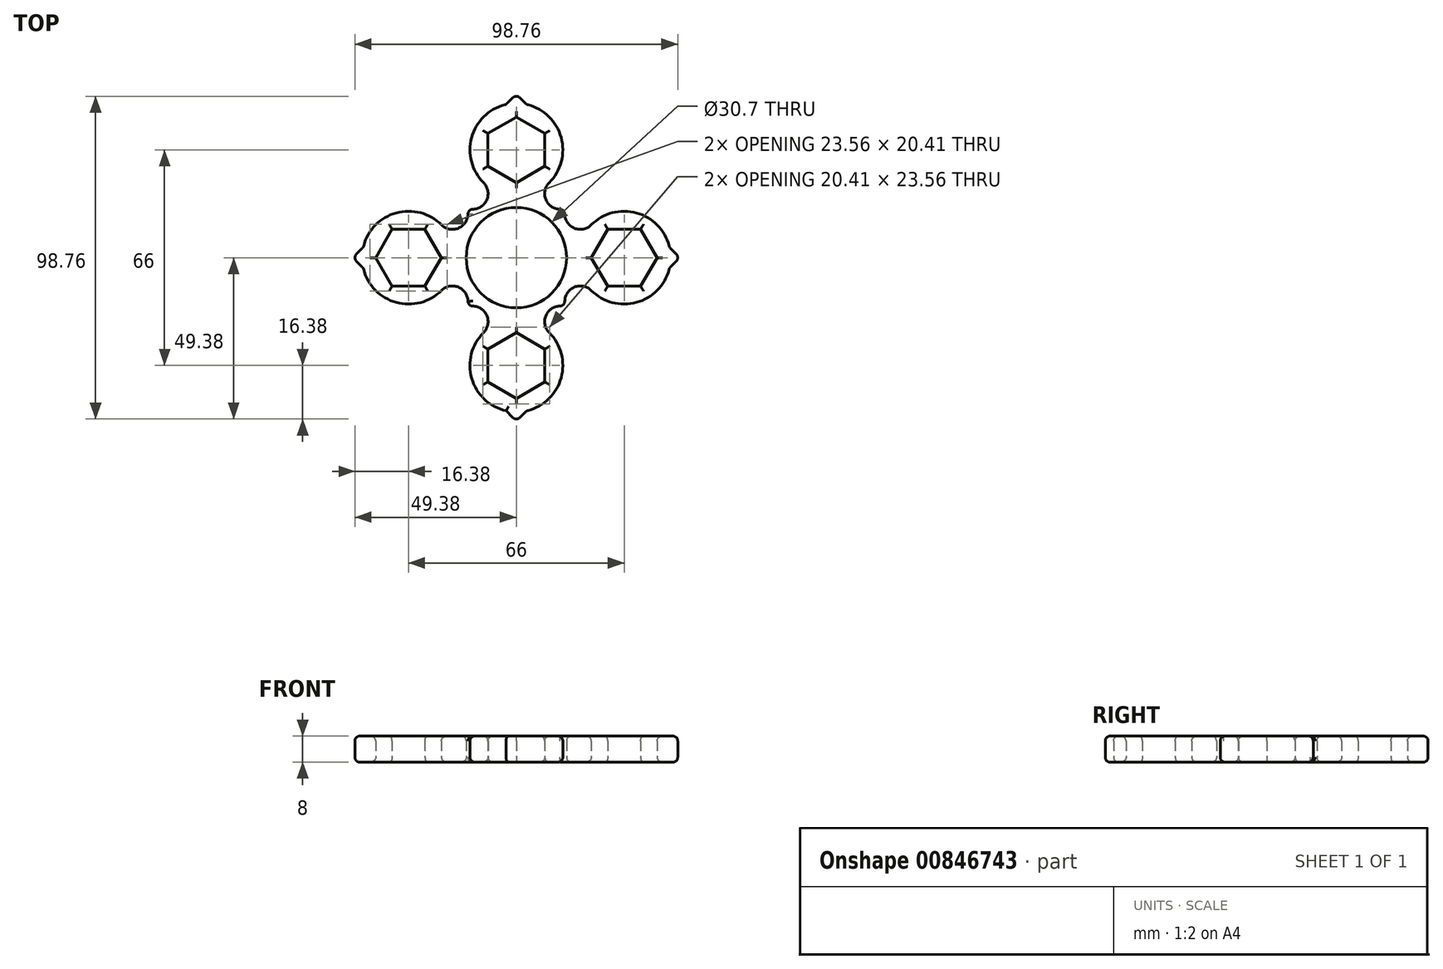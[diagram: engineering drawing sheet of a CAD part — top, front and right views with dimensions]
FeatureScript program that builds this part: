
annotation { "Feature Type Name" : "Feature", "Feature Type Description" : "" }
export const myFeature = defineFeature(function(context is Context, id is Id, definition is map)
    precondition{}
    {
        {
            var Q0;
            Q0=qCreatedBy(makeId("Top.planeOp"),FACE);
            var sketch = newSketch(context, id + "F0", { "sketchPlane" : qUnion([Q0])});
            skCircle(sketch, "E0", {"center": v(0, 0) * mm, "radius": 15.35 * mm});
            skCircle(sketch, "E1.cCircle", {"center": v(0, 0) * mm, "radius": 50 * mm, "construction": true});
            skLineSegment(sketch, "E1.0", {"start": v(0, 50) * mm, "end": v(3.14, 46.86) * mm});
            skLineSegment(sketch, "E1.1", {"start": v(50, 0) * mm, "end": v(46.86, -3.14) * mm});
            skLineSegment(sketch, "E1.2", {"start": v(0, -50) * mm, "end": v(-3.14, -46.86) * mm});
            skLineSegment(sketch, "E1.3", {"start": v(-50, 0) * mm, "end": v(-46.86, 3.14) * mm});
            skArc(sketch, "E2.cCircle", {"start": v(8.7, 27.97) * mm, "mid": v(-7.97, 39.12) * mm, "end": v(7.1, 25.9) * mm, "construction": true});
            skLineSegment(sketch, "E2.0", {"start": v(0, 22.95) * mm, "end": v(-8.7, 27.98) * mm});
            skLineSegment(sketch, "E2.1", {"start": v(-8.7, 27.98) * mm, "end": v(-8.7, 38.03) * mm});
            skLineSegment(sketch, "E2.2", {"start": v(-8.7, 38.03) * mm, "end": v(0, 43.05) * mm});
            skLineSegment(sketch, "E2.3", {"start": v(0, 43.05) * mm, "end": v(8.7, 38.03) * mm});
            skLineSegment(sketch, "E2.4", {"start": v(8.7, 38.03) * mm, "end": v(8.7, 27.97) * mm});
            skLineSegment(sketch, "E2.5", {"start": v(8.7, 27.97) * mm, "end": v(0, 22.95) * mm});
            skCircle(sketch, "E3.cCircle", {"center": v(33, 0) * mm, "radius": 10.05 * mm, "construction": true});
            skLineSegment(sketch, "E3.0", {"start": v(22.95, 0) * mm, "end": v(27.98, 8.7) * mm});
            skLineSegment(sketch, "E3.1", {"start": v(27.98, 8.7) * mm, "end": v(38.02, 8.7) * mm});
            skLineSegment(sketch, "E3.2", {"start": v(38.02, 8.7) * mm, "end": v(43.05, 0) * mm});
            skLineSegment(sketch, "E3.3", {"start": v(43.05, 0) * mm, "end": v(38.03, -8.7) * mm});
            skLineSegment(sketch, "E3.4", {"start": v(38.03, -8.7) * mm, "end": v(27.98, -8.7) * mm});
            skLineSegment(sketch, "E3.5", {"start": v(27.97, -8.7) * mm, "end": v(22.95, 0) * mm});
            skCircle(sketch, "E4.cCircle", {"center": v(0, -33) * mm, "radius": 10.05 * mm, "construction": true});
            skLineSegment(sketch, "E4.0", {"start": v(0, -22.95) * mm, "end": v(8.7, -27.97) * mm});
            skLineSegment(sketch, "E4.1", {"start": v(8.7, -27.97) * mm, "end": v(8.7, -38.02) * mm});
            skLineSegment(sketch, "E4.2", {"start": v(8.7, -38.02) * mm, "end": v(0, -43.05) * mm});
            skLineSegment(sketch, "E4.3", {"start": v(0, -43.05) * mm, "end": v(-8.7, -38.03) * mm});
            skLineSegment(sketch, "E4.4", {"start": v(-8.7, -38.03) * mm, "end": v(-8.7, -27.98) * mm});
            skLineSegment(sketch, "E4.5", {"start": v(-8.7, -27.98) * mm, "end": v(0, -22.95) * mm});
            skCircle(sketch, "E5.cCircle", {"center": v(-33, 0) * mm, "radius": 10.05 * mm, "construction": true});
            skLineSegment(sketch, "E5.0", {"start": v(-22.95, 0) * mm, "end": v(-27.98, -8.7) * mm});
            skLineSegment(sketch, "E5.1", {"start": v(-27.98, -8.7) * mm, "end": v(-38.03, -8.7) * mm});
            skLineSegment(sketch, "E5.2", {"start": v(-38.02, -8.7) * mm, "end": v(-43.05, 0) * mm});
            skLineSegment(sketch, "E5.3", {"start": v(-43.05, 0) * mm, "end": v(-38.03, 8.7) * mm});
            skLineSegment(sketch, "E5.4", {"start": v(-38.03, 8.7) * mm, "end": v(-27.97, 8.7) * mm});
            skLineSegment(sketch, "E5.5", {"start": v(-27.97, 8.7) * mm, "end": v(-22.95, 0) * mm});
            skPoint(sketch, "E6.center.orphan", {"position": v(16.5, 16.5) * mm});
            skArc(sketch, "E7", {"start": v(15.14, -15.14) * mm, "mid": v(9.43, -16.98) * mm, "end": v(10.05, -22.95) * mm});
            skArc(sketch, "E8", {"start": v(22.95, -10.05) * mm, "mid": v(16.98, -9.43) * mm, "end": v(15.14, -15.14) * mm});
            skArc(sketch, "E9", {"start": v(15.14, 15.14) * mm, "mid": v(16.98, 9.43) * mm, "end": v(22.95, 10.05) * mm});
            skArc(sketch, "E10", {"start": v(10.05, 22.95) * mm, "mid": v(9.43, 16.98) * mm, "end": v(15.14, 15.14) * mm});
            skArc(sketch, "E11", {"start": v(-22.95, 10.05) * mm, "mid": v(-16.98, 9.43) * mm, "end": v(-15.14, 15.14) * mm});
            skArc(sketch, "E12", {"start": v(-15.14, -15.14) * mm, "mid": v(-16.98, -9.43) * mm, "end": v(-22.95, -10.05) * mm});
            skArc(sketch, "E13", {"start": v(-10.05, -22.95) * mm, "mid": v(-9.43, -16.98) * mm, "end": v(-15.14, -15.14) * mm});
            skArc(sketch, "E14", {"start": v(-22.95, 10.05) * mm, "mid": v(-36.94, 13.65) * mm, "end": v(-46.86, 3.14) * mm});
            skArc(sketch, "E15", {"start": v(-10.05, -22.95) * mm, "mid": v(-13.65, -36.94) * mm, "end": v(-3.14, -46.86) * mm});
            skArc(sketch, "E16", {"start": v(22.95, -10.05) * mm, "mid": v(36.94, -13.65) * mm, "end": v(46.86, -3.14) * mm});
            skArc(sketch, "E17.trimOffspring", {"start": v(10.05, 22.95) * mm, "mid": v(13.65, 36.94) * mm, "end": v(3.14, 46.86) * mm});
            skLineSegment(sketch, "E18.trimOffspring", {"start": v(46.86, 3.14) * mm, "end": v(50, 0) * mm});
            skLineSegment(sketch, "E19.trimOffspring", {"start": v(-3.14, 46.86) * mm, "end": v(0, 50) * mm});
            skArc(sketch, "E20.trimOffspring", {"start": v(-3.14, 46.86) * mm, "mid": v(-13.65, 36.94) * mm, "end": v(-10.05, 22.95) * mm});
            skLineSegment(sketch, "E21.trimOffspring", {"start": v(-46.86, -3.14) * mm, "end": v(-50, 0) * mm});
            skLineSegment(sketch, "E22.trimOffspring", {"start": v(3.14, -46.86) * mm, "end": v(0, -50) * mm});
            skArc(sketch, "E23.trimOffspring", {"start": v(-46.86, -3.14) * mm, "mid": v(-36.94, -13.65) * mm, "end": v(-22.95, -10.05) * mm});
            skPoint(sketch, "E24.center.orphan", {"position": v(-16.5, 16.5) * mm});
            skArc(sketch, "E25.trimOffspring", {"start": v(-15.14, 15.14) * mm, "mid": v(-9.43, 16.98) * mm, "end": v(-10.05, 22.95) * mm});
            skPoint(sketch, "E26.center.orphan", {"position": v(-16.5, -16.5) * mm});
            skArc(sketch, "E27.trimOffspring", {"start": v(3.14, -46.86) * mm, "mid": v(13.65, -36.94) * mm, "end": v(10.05, -22.95) * mm});
            skLineSegment(sketch, "E28", {"start": v(10.06, -22.94) * mm, "end": v(10.05, -22.95) * mm});
            skPoint(sketch, "E29.center.orphan", {"position": v(16.5, -16.5) * mm});
            skArc(sketch, "E30.trimOffspring", {"start": v(46.86, 3.14) * mm, "mid": v(36.94, 13.65) * mm, "end": v(22.95, 10.05) * mm});
            skSolve(sketch);
        }
        {
            var Q0;
            Q0 = qSketchRegion(id + "F0", true);
            extrude(context, id + "F1", {"entities" : qUnion([Q0]), "depth" : 8 * mm, "offsetDistance" : 25 * mm});
        }
        {
            var Q0;
            Q0=makeQuery(id+"F1.opExtrude","CAP_FACE",FACE,{"disambiguationData":[OSD([sQuery(id+"F0.wireOp",EDGE,"E0"),sQuery(id+"F0.wireOp",EDGE,"E1.0"),sQuery(id+"F0.wireOp",EDGE,"E1.1"),sQuery(id+"F0.wireOp",EDGE,"E1.2"),sQuery(id+"F0.wireOp",EDGE,"E1.3"),sQuery(id+"F0.wireOp",EDGE,"E2.0"),sQuery(id+"F0.wireOp",EDGE,"E2.1"),sQuery(id+"F0.wireOp",EDGE,"E2.2"),sQuery(id+"F0.wireOp",EDGE,"E2.3"),sQuery(id+"F0.wireOp",EDGE,"E2.4"),sQuery(id+"F0.wireOp",EDGE,"E2.5"),sQuery(id+"F0.wireOp",EDGE,"E3.0"),sQuery(id+"F0.wireOp",EDGE,"E3.1"),sQuery(id+"F0.wireOp",EDGE,"E3.2"),sQuery(id+"F0.wireOp",EDGE,"E3.3"),sQuery(id+"F0.wireOp",EDGE,"E3.4"),sQuery(id+"F0.wireOp",EDGE,"E3.5"),sQuery(id+"F0.wireOp",EDGE,"E4.0"),sQuery(id+"F0.wireOp",EDGE,"E4.1"),sQuery(id+"F0.wireOp",EDGE,"E4.2"),sQuery(id+"F0.wireOp",EDGE,"E4.3"),sQuery(id+"F0.wireOp",EDGE,"E4.4"),sQuery(id+"F0.wireOp",EDGE,"E4.5"),sQuery(id+"F0.wireOp",EDGE,"E5.0"),sQuery(id+"F0.wireOp",EDGE,"E5.1"),sQuery(id+"F0.wireOp",EDGE,"E5.2"),sQuery(id+"F0.wireOp",EDGE,"E5.3"),sQuery(id+"F0.wireOp",EDGE,"E5.4"),sQuery(id+"F0.wireOp",EDGE,"E5.5"),sQuery(id+"F0.wireOp",EDGE,"E7"),sQuery(id+"F0.wireOp",EDGE,"E8"),sQuery(id+"F0.wireOp",EDGE,"E9"),sQuery(id+"F0.wireOp",EDGE,"E10"),sQuery(id+"F0.wireOp",EDGE,"E11"),sQuery(id+"F0.wireOp",EDGE,"E12"),sQuery(id+"F0.wireOp",EDGE,"E13"),sQuery(id+"F0.wireOp",EDGE,"E14"),sQuery(id+"F0.wireOp",EDGE,"E15"),sQuery(id+"F0.wireOp",EDGE,"E16"),sQuery(id+"F0.wireOp",EDGE,"E17.trimOffspring"),sQuery(id+"F0.wireOp",EDGE,"E18.trimOffspring"),sQuery(id+"F0.wireOp",EDGE,"E19.trimOffspring"),sQuery(id+"F0.wireOp",EDGE,"E20.trimOffspring"),sQuery(id+"F0.wireOp",EDGE,"E21.trimOffspring"),sQuery(id+"F0.wireOp",EDGE,"E22.trimOffspring"),sQuery(id+"F0.wireOp",EDGE,"E23.trimOffspring"),sQuery(id+"F0.wireOp",EDGE,"E25.trimOffspring"),sQuery(id+"F0.wireOp",EDGE,"E27.trimOffspring"),sQuery(id+"F0.wireOp",EDGE,"E30.trimOffspring")])],"isStart":false});
            var Q1;
            Q1=makeQuery(id+"F1.opExtrude","CAP_FACE",FACE,{"disambiguationData":[OSD([sQuery(id+"F0.wireOp",EDGE,"E0"),sQuery(id+"F0.wireOp",EDGE,"E1.0"),sQuery(id+"F0.wireOp",EDGE,"E1.1"),sQuery(id+"F0.wireOp",EDGE,"E1.2"),sQuery(id+"F0.wireOp",EDGE,"E1.3"),sQuery(id+"F0.wireOp",EDGE,"E2.0"),sQuery(id+"F0.wireOp",EDGE,"E2.1"),sQuery(id+"F0.wireOp",EDGE,"E2.2"),sQuery(id+"F0.wireOp",EDGE,"E2.3"),sQuery(id+"F0.wireOp",EDGE,"E2.4"),sQuery(id+"F0.wireOp",EDGE,"E2.5"),sQuery(id+"F0.wireOp",EDGE,"E3.0"),sQuery(id+"F0.wireOp",EDGE,"E3.1"),sQuery(id+"F0.wireOp",EDGE,"E3.2"),sQuery(id+"F0.wireOp",EDGE,"E3.3"),sQuery(id+"F0.wireOp",EDGE,"E3.4"),sQuery(id+"F0.wireOp",EDGE,"E3.5"),sQuery(id+"F0.wireOp",EDGE,"E4.0"),sQuery(id+"F0.wireOp",EDGE,"E4.1"),sQuery(id+"F0.wireOp",EDGE,"E4.2"),sQuery(id+"F0.wireOp",EDGE,"E4.3"),sQuery(id+"F0.wireOp",EDGE,"E4.4"),sQuery(id+"F0.wireOp",EDGE,"E4.5"),sQuery(id+"F0.wireOp",EDGE,"E5.0"),sQuery(id+"F0.wireOp",EDGE,"E5.1"),sQuery(id+"F0.wireOp",EDGE,"E5.2"),sQuery(id+"F0.wireOp",EDGE,"E5.3"),sQuery(id+"F0.wireOp",EDGE,"E5.4"),sQuery(id+"F0.wireOp",EDGE,"E5.5"),sQuery(id+"F0.wireOp",EDGE,"E7"),sQuery(id+"F0.wireOp",EDGE,"E8"),sQuery(id+"F0.wireOp",EDGE,"E9"),sQuery(id+"F0.wireOp",EDGE,"E10"),sQuery(id+"F0.wireOp",EDGE,"E11"),sQuery(id+"F0.wireOp",EDGE,"E12"),sQuery(id+"F0.wireOp",EDGE,"E13"),sQuery(id+"F0.wireOp",EDGE,"E14"),sQuery(id+"F0.wireOp",EDGE,"E15"),sQuery(id+"F0.wireOp",EDGE,"E16"),sQuery(id+"F0.wireOp",EDGE,"E17.trimOffspring"),sQuery(id+"F0.wireOp",EDGE,"E18.trimOffspring"),sQuery(id+"F0.wireOp",EDGE,"E19.trimOffspring"),sQuery(id+"F0.wireOp",EDGE,"E20.trimOffspring"),sQuery(id+"F0.wireOp",EDGE,"E21.trimOffspring"),sQuery(id+"F0.wireOp",EDGE,"E22.trimOffspring"),sQuery(id+"F0.wireOp",EDGE,"E23.trimOffspring"),sQuery(id+"F0.wireOp",EDGE,"E25.trimOffspring"),sQuery(id+"F0.wireOp",EDGE,"E27.trimOffspring"),sQuery(id+"F0.wireOp",EDGE,"E30.trimOffspring")])],"isStart":true});
            var Q2;
            Q2=makeQuery(id+"F1.opExtrude","SWEPT_EDGE",EDGE,{"disambiguationData":[OSD([sQuery(id+"F0.wireOp",EDGE,"E22.trimOffspring"),sQuery(id+"F0.wireOp",EDGE,"E27.trimOffspring")])]});
            var Q3;
            Q3=makeQuery(id+"F1.opExtrude","SWEPT_EDGE",EDGE,{"disambiguationData":[OSD([sQuery(id+"F0.wireOp",EDGE,"E1.2"),sQuery(id+"F0.wireOp",EDGE,"E22.trimOffspring")])]});
            var Q4;
            Q4=makeQuery(id+"F1.opExtrude","CAP_EDGE",EDGE,{"disambiguationData":[OSD([sQuery(id+"F0.wireOp",EDGE,"E1.2")])],"isStart":true});
            var Q5;
            Q5=makeQuery(id+"F1.opExtrude","SWEPT_EDGE",EDGE,{"disambiguationData":[OSD([sQuery(id+"F0.wireOp",EDGE,"E7"),sQuery(id+"F0.wireOp",EDGE,"E8")])]});
            var Q6;
            Q6=makeQuery(id+"F1.opExtrude","SWEPT_EDGE",EDGE,{"disambiguationData":[OSD([sQuery(id+"F0.wireOp",EDGE,"E12"),sQuery(id+"F0.wireOp",EDGE,"E13")])]});
            var Q7;
            Q7=makeQuery(id+"F1.opExtrude","SWEPT_EDGE",EDGE,{"disambiguationData":[OSD([sQuery(id+"F0.wireOp",EDGE,"E21.trimOffspring"),sQuery(id+"F0.wireOp",EDGE,"E23.trimOffspring")])]});
            var Q8;
            Q8=makeQuery(id+"F1.opExtrude","SWEPT_EDGE",EDGE,{"disambiguationData":[OSD([sQuery(id+"F0.wireOp",EDGE,"E1.3"),sQuery(id+"F0.wireOp",EDGE,"E21.trimOffspring")])]});
            var Q9;
            Q9=makeQuery(id+"F1.opExtrude","SWEPT_EDGE",EDGE,{"disambiguationData":[OSD([sQuery(id+"F0.wireOp",EDGE,"E1.3"),sQuery(id+"F0.wireOp",EDGE,"E14")])]});
            var Q10;
            Q10=makeQuery(id+"F1.opExtrude","SWEPT_EDGE",EDGE,{"disambiguationData":[OSD([sQuery(id+"F0.wireOp",EDGE,"E11"),sQuery(id+"F0.wireOp",EDGE,"E25.trimOffspring")])]});
            var Q11;
            Q11=makeQuery(id+"F1.opExtrude","SWEPT_EDGE",EDGE,{"disambiguationData":[OSD([sQuery(id+"F0.wireOp",EDGE,"E1.0"),sQuery(id+"F0.wireOp",EDGE,"E19.trimOffspring")])]});
            var Q12;
            Q12=makeQuery(id+"F1.opExtrude","SWEPT_EDGE",EDGE,{"disambiguationData":[OSD([sQuery(id+"F0.wireOp",EDGE,"E19.trimOffspring"),sQuery(id+"F0.wireOp",EDGE,"E20.trimOffspring")])]});
            var Q13;
            Q13=makeQuery(id+"F1.opExtrude","SWEPT_EDGE",EDGE,{"disambiguationData":[OSD([sQuery(id+"F0.wireOp",EDGE,"E1.0"),sQuery(id+"F0.wireOp",EDGE,"E17.trimOffspring")])]});
            var Q14;
            Q14=makeQuery(id+"F1.opExtrude","SWEPT_EDGE",EDGE,{"disambiguationData":[OSD([sQuery(id+"F0.wireOp",EDGE,"E9"),sQuery(id+"F0.wireOp",EDGE,"E10")])]});
            var Q15;
            Q15=makeQuery(id+"F1.opExtrude","SWEPT_EDGE",EDGE,{"disambiguationData":[OSD([sQuery(id+"F0.wireOp",EDGE,"E18.trimOffspring"),sQuery(id+"F0.wireOp",EDGE,"E30.trimOffspring")])]});
            var Q16;
            Q16=makeQuery(id+"F1.opExtrude","SWEPT_EDGE",EDGE,{"disambiguationData":[OSD([sQuery(id+"F0.wireOp",EDGE,"E1.1"),sQuery(id+"F0.wireOp",EDGE,"E18.trimOffspring")])]});
            var Q17;
            Q17=makeQuery(id+"F1.opExtrude","SWEPT_EDGE",EDGE,{"disambiguationData":[OSD([sQuery(id+"F0.wireOp",EDGE,"E1.1"),sQuery(id+"F0.wireOp",EDGE,"E16")])]});
            fillet(context, id + "F2", {"entities" : qUnion([Q0, Q1, Q2, Q3, Q4, Q5, Q6, Q7, Q8, Q9, Q10, Q11, Q12, Q13, Q14, Q15, Q16, Q17]), "radius" : 1.5 * mm, "tangentPropagation" : true, "allowEdgeOverflow" : false});
        }
    });
